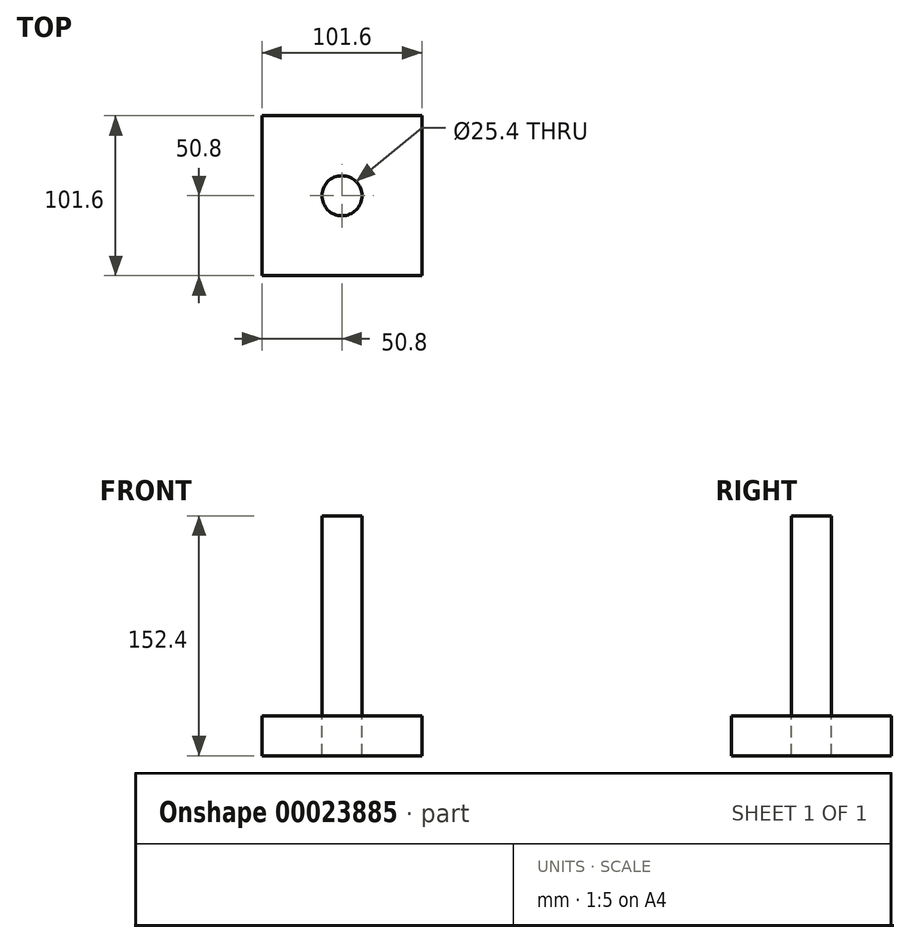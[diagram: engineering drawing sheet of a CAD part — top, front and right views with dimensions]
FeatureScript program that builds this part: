
annotation { "Feature Type Name" : "Feature", "Feature Type Description" : "" }
export const myFeature = defineFeature(function(context is Context, id is Id, definition is map)
    precondition{}
    {
        {
            var Q0;
            Q0=qCreatedBy(makeId("Top.planeOp"),FACE);
            var sketch = newSketch(context, id + "F0", { "sketchPlane" : qUnion([Q0])});
            skCircle(sketch, "E0", {"center": v(0, 0) * mm, "radius": 12.7 * mm});
            skSolve(sketch);
        }
        {
            var Q0;
            Q0=makeQuery(id+"F0.imprint","IMPRINT",FACE,{"disambiguationData":[TD([[makeQuery(id+"F0.imprint","IMPRINT",EDGE,{"derivedFrom":sQuery(id+"F0.wireOp",EDGE,"E0")}),1.0]])]});
            extrude(context, id + "F1", {"entities" : qUnion([Q0]), "depth" : 127 * mm});
        }
        {
            var Q0;
            Q0=qCreatedBy(makeId("Top.planeOp"),FACE);
            var sketch = newSketch(context, id + "F2", { "sketchPlane" : qUnion([Q0])});
            skCircle(sketch, "E1", {"center": v(0, 0) * mm, "radius": 12.7 * mm});
            skLineSegment(sketch, "E2.rect.bottom", {"start": v(50.8, -50.8) * mm, "end": v(-50.8, -50.8) * mm});
            skLineSegment(sketch, "E2.rect.top", {"start": v(50.8, 50.8) * mm, "end": v(-50.8, 50.8) * mm});
            skLineSegment(sketch, "E2.rect.left", {"start": v(50.8, -50.8) * mm, "end": v(50.8, 50.8) * mm});
            skLineSegment(sketch, "E2.rect.right", {"start": v(-50.8, -50.8) * mm, "end": v(-50.8, 50.8) * mm});
            skSolve(sketch);
        }
        {
            var Q0;
            Q0=makeQuery(id+"F2.imprint","IMPRINT",FACE,{"disambiguationData":[TD([[makeQuery(id+"F2.imprint","IMPRINT",EDGE,{"derivedFrom":sQuery(id+"F2.wireOp",EDGE,"E1")}),-1.0]])]});
            extrude(context, id + "F3", {"entities" : qUnion([Q0]), "oppositeDirection" : true, "depth" : 25.4 * mm});
        }
    });
